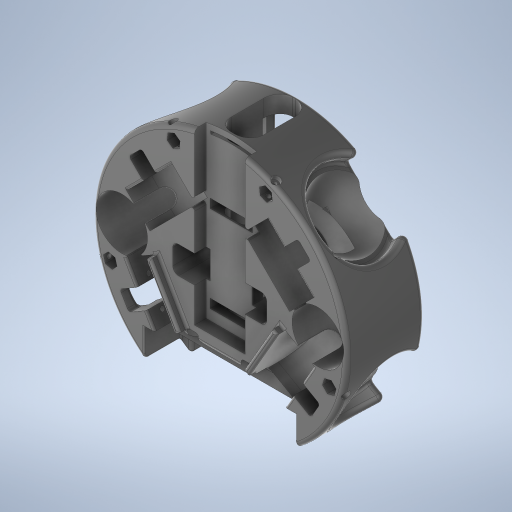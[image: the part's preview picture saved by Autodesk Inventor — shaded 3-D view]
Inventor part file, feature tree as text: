
AUTODESK INVENTOR PART (.ipt)
format: ipt  version: 2023 (Build 270158000, 158)  size: 3,526,144 bytes
history: native  units: mm
features: extrude x76, sketch x76, projected_geometry x35, fillet x19, other x16, chamfer x4, plane x2, mirror x2
ambient origin geometry x8: Origin, YZ Plane, XZ Plane, XY Plane, X Axis, Y Axis, Z Axis, Center Point
bodies: Solid1 (feature_tree)
feature tree (230):
  extrude  "Cilinder"  Depth=54.0mm TaperAngle=0.0deg
  other  "Motor Axis"
  other  "Plano M1"
  other  "Plano M2"
  other  "Plano M3"
  other  "Plano M4"
  extrude  "Roda M1"  Depth=176.0mm
  extrude  "Roda M2"  TaperAngle=60.0deg  [1 undecoded]
  extrude  "Roda M3"  TaperAngle=45.0deg  [1 undecoded]
  extrude  "Roda M4"  TaperAngle=0.0deg  [1 undecoded]
  extrude  "MotorsFitting"  Depth=14.6mm TaperAngle=0.0deg
  fillet  "MotorsCurve"  Radius=55.0mm
  extrude  "Threads M1"  Depth=20.0mm
  extrude  "Threads M2"  Depth=55.0mm
  extrude  "Threads M3"  Depth=20.0mm
  extrude  "Threads M4"  Depth=55.0mm
  extrude  "Threads Head M1"  Depth=20.0mm
  extrude  "Threads Head M2"  Depth=9.4mm
  extrude  "Threads Head M3"  Depth=9.4mm
  extrude  "Threads Head M4"  Depth=23.0mm
  extrude  "Thread Depth M1"  Depth=9.4mm
  extrude  "Thread Depth M2"  Depth=45.0mm
  extrude  "Thread Depth M3"  Depth=45.0mm
  extrude  "Thread Depth M4"  Depth=30.0mm
  extrude  "Threads Nut Head M1"  Depth=32.5mm
  extrude  "Threads Nut Head M2"  Depth=40.0mm TaperAngle=0.0deg
  extrude  "Threads Nut Head M3"  Depth=5.0mm
  extrude  "Threads Nut Head M4"  TaperAngle=0.0deg  [1 undecoded]
  extrude  "Wheel Fitting M1"  Depth=3.0mm
  extrude  "Wheel Fitting M2"  TaperAngle=0.0deg  [1 undecoded]
  extrude  "Wheel Fitting M3"  Depth=30.0mm TaperAngle=360.0deg
  extrude  "Wheel Fitting M4"  Depth=2.0mm
  extrude  "Capacitors"  Depth=6.0mm
  extrude  "Gear Entrance M1"  Depth=19.5mm
  extrude  "Gear Entrance M2"  Depth=10.0mm
  extrude  "Gear Entrance M3"  Depth=2.0mm
  extrude  "Gear Entrance M4"  Depth=3.0mm
  fillet  "Rounding Edges"  Radius=3.0mm
  fillet  "Rounding Motor Entrances"  Radius=6.0mm
  extrude  "Standoff Fitting"  TaperAngle=0.0deg  [1 undecoded]
  extrude  "Standoff Thread M1"  Depth=19.6mm
  extrude  "Standoff Thread M2"  Depth=19.5mm
  extrude  "Standoff Thread M3"  TaperAngle=0.0deg  [1 undecoded]
  extrude  "Standoff Thread M4"  Depth=30.0mm TaperAngle=360.0deg
  other  "Standoff Plane M1"
  other  "Standoff Plane M2"
  other  "Standoff Plane M3"
  other  "Standoff Plane M4"
  extrude  "Standoff Head M1"  Depth=10.0mm
  extrude  "Standoff Head M2"  Depth=2.0mm
  extrude  "Standoff Head M3"  TaperAngle=0.0deg  [1 undecoded]
  extrude  "Standoff Head M4"  Depth=6.0mm
  extrude  "Dribbler Entrance"  Depth=19.5mm
  extrude  "Battery Fitting"  Depth=3.0mm
  fillet  "Motor to Battery Edges"  Radius=3.0mm
  extrude  "Front Kicker"  Depth=11.0mm
  fillet  "Front Edges"  Radius=30.0mm
  extrude  "Cover Inlet"  Depth=10.0mm TaperAngle=0.0deg
  extrude  "Capacitors Holes"  Depth=2.0mm
  extrude  "Dribbler Motor Space"  Depth=6.0mm
  extrude  "IR Holder"  TaperAngle=0.0deg  [1 undecoded]
  fillet  "Dribbler and Kicker Edges"  Radius=19.5mm
  fillet  "Minor Fixes"  Radius=19.5mm
  chamfer  "Dribbler Chanfer"  Distance=30.0mm Angle=360.0deg
  extrude  "Capacitor Cable Fittng 1"  Depth=10.0mm TaperAngle=0.0deg
  fillet  "Capacitor Cable Rounding"  Radius=5.5mm
  extrude  "Special Nut M1"  Depth=5.5mm
  extrude  "Special Nut M2"  Depth=5.5mm
  extrude  "Special Nut M3"  Depth=5.5mm
  extrude  "Special Nut M4"  Depth=5.5mm
  extrude  "Special Nut Cylinder M1"  Depth=5.5mm
  extrude  "Special Nut Cylinder M2"  Depth=5.5mm
  extrude  "Special Nut Cylinder M3"  Depth=5.5mm
  extrude  "Special Nut Cylinder M4"  Depth=4.0mm
  fillet  "Special Nut Rounding"  Radius=4.0mm
  extrude  "Kicker Plate Fit 1"  Depth=4.0mm
  extrude  "Kicker Front Opening"  Depth=17.75mm TaperAngle=0.0deg
  extrude  "Kicker Base Fit"  Depth=4.0mm
  extrude  "Coil and Plinge Fitting"  Depth=4.0mm
  extrude  "Kicker Pkate Plunge Fit"  Depth=17.75mm TaperAngle=0.0deg
  chamfer  "Plunge Entrance 1"  Distance=17.6mm
  chamfer  "Plunge Entrance 2"  Distance=17.6mm
  fillet  "Fillet11"  Radius=15.5mm
  chamfer  "Coil Edges 1"  Distance=17.6mm
  extrude  "Kicker Plate Threads"  Depth=32.0mm
  extrude  "kicker Plate Nut 1"  Depth=35.7mm
  extrude  "Kicker Plate Nut 2"  Depth=68.0mm
  extrude  "Kicker Plunge Fit"  Depth=10.0mm TaperAngle=0.0deg
  fillet  "Kicker Plunge Round"  Radius=12.5mm
  fillet  "Wheel Round"  Radius=14.0mm
  extrude  "Capacitor Cables"  Depth=10.0mm
  fillet  "Capacitor Cable Round 1"  Radius=12.5mm
  fillet  "Capacitor Cable Round 2"  Radius=10.0mm
  extrude  "MotorProtection"  Depth=10.0mm TaperAngle=0.0deg
  fillet  "Motor Protection Round"  Radius=12.5mm
  extrude  "Extrusion86"  Depth=10.0mm
  extrude  "Extrusion87"  Depth=10.0mm TaperAngle=0.0deg
  fillet  "Fillet17"  Radius=12.5mm
  extrude  "Extrusion88"  Depth=10.0mm
  plane  "Work Plane14"
  extrude  "Extrusion89"  Depth=10.0mm TaperAngle=0.0deg
  extrude  "Extrusion91"  Depth=3.0mm
  mirror  "Mirror3"
  fillet  "Fillet18"  Radius=2.0mm
  extrude  "Extrusion92"  Depth=10.0mm
  fillet  "Fillet19"  Radius=22.0mm
  extrude  "Extrusion93"  Depth=10.0mm
  fillet  "Fillet20"  Radius=4.22mm
  extrude  "Extrusion94"  Depth=10.0mm
  extrude  "Extrusion95"  Depth=10.0mm
  other  "Eixo de trabalho1"
  other  "Eixo de trabalho2"
  other  "Eixo de trabalho3"
  other  "Eixo de trabalho4"
  other  "Plano de trabalho16"
  other  "Revolução1"
  other  "Revolução2"
  mirror  "Espelhamento5"
  sketch  "Sketch1"  dims[d0=176.0mm d1=54.0mm d2=0.0mm]
  sketch  "Sketch3"  dims[d3=180.0mm d4=176.0mm]
  sketch  "Sketch4"  dims[d5=60.0deg d6=60.0deg]
  sketch  "Sketch5"  dims[d8=45.0deg d9=45.0deg]
  sketch  "Sketch6"  dims[d10=55.0mm d11=0.0mm]
  sketch  "Sketch7"  dims[d12=20.0mm d13=14.6mm d14=0.0mm d15=55.0mm]
  sketch  "Sketch8"  dims[d16=0.0mm d17=20.0mm]
  sketch  "Sketch9"  dims[d18=14.6mm d19=0.0mm d20=55.0mm]
  sketch  "Sketch10"  dims[d21=0.0mm d22=20.0mm]
  sketch  "Sketch11"  dims[d23=14.6mm d24=0.0mm d25=55.0mm]
  sketch  "Sketch12"  dims[d26=0.0mm d27=20.0mm]
  sketch  "Sketch13"  dims[d28=14.6mm d29=0.0mm d30=9.4mm]
  sketch  "Sketch14"  dims[d32=9.4mm d33=9.4mm]
  sketch  "Sketch15"  dims[d34=23.0mm d35=23.0mm]
  sketch  "Sketch16"  dims[d37=23.0mm d38=9.4mm]
  sketch  "Sketch17"  dims[d39=23.0mm d40=45.0mm]
  sketch  "Sketch18"  dims[d41=45.0mm d42=45.0mm]
  sketch  "Sketch19"  dims[d43=45.0mm d44=30.0mm]
  sketch  "Sketch20"  dims[d45=30.0mm d46=32.5mm]
  sketch  "Sketch21"  dims[d47=32.5mm d48=40.0mm d49=0.0mm]
  sketch  "Sketch22"  dims[d50=22.5mm d51=5.0mm]
  sketch  "Sketch23"  dims[d52=12.5mm d53=0.0mm]
  sketch  "Sketch24"  dims[d54=19.5mm d55=3.0mm]
  sketch  "Sketch25"  dims[d56=19.6mm d58=0.0mm]
  sketch  "Sketch26"  dims[d59=11.0mm d60=30.0mm d62=360.0deg]
  sketch  "Sketch27"  dims[d64=2.0mm d65=2.0mm]
  sketch  "Sketch28"  dims[d66=6.0mm d67=6.0mm]
  sketch  "Sketch29"  dims[d68=19.5mm d69=19.5mm]
  sketch  "Sketch30"  dims[d70=10.0mm d71=0.0mm d72=2.5mm]
  projected_geometry  "Projected Loop1"
  sketch  "Sketch31"  dims[d73=5.0mm d74=2.0mm]
  projected_geometry  "Projected Loop2"
  sketch  "Sketch32"  dims[d75=2.0mm d76=12.5mm d77=3.0mm d78=6.0mm]
  projected_geometry  "Projected Loop3"
  sketch  "Sketch33"  dims[d79=6.0mm d80=0.0mm]
  projected_geometry  "Projected Loop4"
  sketch  "Sketch34"  dims[d81=19.5mm d82=19.6mm]
  sketch  "Sketch35"  dims[d83=19.5mm d84=19.5mm]
  projected_geometry  "Projected Loop5"
  sketch  "Sketch36"  dims[d85=5.0mm d86=0.0mm]
  projected_geometry  "Projected Loop6"
  sketch  "Sketch37"  dims[d87=11.0mm d88=30.0mm d90=360.0deg]
  projected_geometry  "Projected Loop7"
  sketch  "Sketch38"  dims[d92=10.0mm d93=0.0mm d94=5.0mm]
  projected_geometry  "Projected Loop8"
  sketch  "Sketch39"  dims[d95=12.5mm d96=2.0mm]
  sketch  "Sketch40"  dims[d97=2.0mm d98=0.0mm]
  sketch  "Sketch41"  dims[d99=19.5mm d100=6.0mm]
  sketch  "Sketch42"  dims[d101=6.0mm d102=19.5mm]
  sketch  "Sketch43"  dims[d103=19.5mm d104=19.6mm d105=3.0mm]
  sketch  "Sketch44"  dims[d106=0.0mm d107=11.0mm d108=30.0mm d110=360.0deg]
  projected_geometry  "Projected Loop9"
  projected_geometry  "Projected Loop10"
  sketch  "Sketch45"  dims[d112=5.0mm d113=10.0mm d114=0.0mm]
  sketch  "Sketch46"  dims[d115=5.0mm d116=2.0mm]
  projected_geometry  "Projected Loop11"
  projected_geometry  "Projected Loop12"
  sketch  "Sketch48"  dims[d117=2.0mm d118=6.0mm]
  projected_geometry  "Projected Loop14"
  sketch  "Sketch50"  dims[d119=6.0mm d120=0.0mm d121=19.5mm d122=19.5mm]
  projected_geometry  "Projected Loop15"
  sketch  "Sketch59"  dims[d123=19.5mm]
  sketch  "Sketch64"  dims[d124=12.5mm]
  sketch  "Sketch65"  dims[d125=19.6mm]
  projected_geometry  "Projected Loop27"
  sketch  "Sketch66"  dims[d126=3.0mm]
  projected_geometry  "Projected Loop28"
  sketch  "Sketch67"  dims[d127=0.0mm]
  sketch  "Sketch68"  dims[d128=11.0mm d129=30.0mm d131=360.0deg]
  sketch  "Sketch69"  dims[d133=2.5mm d134=10.0mm d135=0.0mm d136=5.5mm]
  sketch  "Sketch70"  dims[d137=5.5mm d138=5.5mm]
  sketch  "Sketch71"  dims[d139=18.0mm d140=0.0mm d141=5.5mm]
  sketch  "Sketch72"  dims[d142=5.5mm d143=5.5mm]
  projected_geometry  "Projected Loop29"
  sketch  "Sketch73"  dims[d144=18.0mm d145=0.0mm d146=5.5mm]
  sketch  "Sketch74"  dims[d147=5.5mm d148=5.5mm]
  projected_geometry  "Projected Loop30"
  sketch  "Sketch75"  dims[d149=18.0mm d150=0.0mm d151=5.5mm]
  projected_geometry  "Projected Loop31"
  sketch  "Sketch76"  dims[d152=5.5mm d153=5.5mm]
  projected_geometry  "Projected Loop32"
  projected_geometry  "Projected Loop33"
  sketch  "Sketch77"  dims[d154=18.0mm d155=0.0mm d156=4.0mm d157=4.0mm]
  projected_geometry  "Projected Loop34"
  projected_geometry  "Projected Loop35"
  projected_geometry  "Projected Loop36"
  projected_geometry  "Projected Loop37"
  sketch  "Sketch78"  dims[d158=17.75mm d159=0.0mm d160=4.0mm]
  sketch  "Sketch80"  dims[d161=4.0mm d162=17.75mm d163=0.0mm]
  projected_geometry  "Projected Loop38"
  projected_geometry  "Projected Loop39"
  projected_geometry  "Projected Loop40"
  projected_geometry  "Projected Loop41"
  sketch  "Sketch81"  dims[d164=4.0mm d165=4.0mm]
  sketch  "Sketch82"  dims[d166=17.75mm d167=0.0mm d168=4.0mm]
  sketch  "Sketch89"  dims[d169=4.0mm d170=17.75mm d171=0.0mm]
  sketch  "Sketch90"  dims[d172=15.5mm]
  sketch  "Sketch92"  dims[d173=32.0mm d174=17.6mm d175=0.0mm]
  sketch  "Sketch93"  dims[d176=15.5mm]
  sketch  "Sketch95"  dims[d177=32.0mm d178=17.6mm d179=0.0mm d180=15.5mm]
  plane  "Work Plane15"
  projected_geometry  "Projected Loop46"
  projected_geometry  "Projected Loop47"
  projected_geometry  "Projected Loop48"
  sketch  "Sketch97"  dims[d181=32.0mm d182=17.6mm d183=0.0mm]
  sketch  "Sketch98"  dims[d184=15.5mm d185=32.0mm]
  projected_geometry  "Projected Loop49"
  projected_geometry  "Projected Loop50"
  projected_geometry  "Projected Loop51"
  sketch  "Sketch99"  dims[d186=17.6mm d187=0.0mm d188=35.7mm]
  sketch  "Esboço100"  dims[d189=4.15mm d190=68.0mm]
  sketch  "Esboço101"  dims[d191=68.0mm d192=50.0mm d193=0.0mm d195=12.5mm d196=14.0mm d197=0.0mm d198=10.0mm d199=12.5mm d200=10.0mm d201=14.0mm d202=0.0mm d203=12.5mm d204=10.0mm d205=14.0mm d206=0.0mm d207=12.5mm d208=10.0mm d209=14.0mm d210=0.0mm d211=3.0mm d212=2.0mm d213=2.0mm d214=2.0mm d215=22.0mm d216=76.0mm d217=4.22mm d218=72.0mm d219=32.0mm d220=4.22mm d221=8.0mm d222=0.0mm d223=3.0mm d224=3.5mm d225=2.436418mm d226=24.0mm d227=0.0mm d228=3.0mm d229=3.5mm d230=2.436418mm d231=24.0mm d232=0.0mm d233=3.0mm d234=3.5mm d235=2.436418mm d236=24.0mm d237=0.0mm d238=3.0mm d239=3.5mm d240=2.436418mm d241=24.0mm d242=0.0mm d243=90.0mm d244=40.0mm d245=0.0mm d246=55.0mm d247=10.0mm d248=0.0mm d249=2.0mm d250=0.0mm d251=2.0mm d252=0.0mm d253=2.0mm d254=0.0mm d255=2.0mm d256=0.0mm d257=2.0mm d258=1.5mm d259=35.0mm d260=120.0mm d261=0.0mm d262=28.5mm d263=8.0mm d264=0.0mm d265=1.5mm d266=-2.0mm d267=-2.0mm d268=-2.0mm d269=-2.0mm d270=5.5mm d271=4.0mm d272=0.0mm d273=5.5mm d274=4.0mm d275=0.0mm d276=5.5mm d277=4.0mm d278=0.0mm d279=5.5mm d280=4.0mm d281=0.0mm d282=56.5mm d283=12.5mm d284=0.0mm d285=17.0mm d286=10.0mm d287=0.0mm d288=2.0mm d289=3.0mm d299=82.0mm d300=17.453293mm d301=3.490659mm d302=84.0mm d303=17.453293mm d304=3.490659mm d305=8.0mm d306=0.0mm d307=0.4mm d308=22.0mm d309=22.0mm d310=10.0mm d311=0.0mm d317=90.0mm d318=14.0mm d319=0.0mm d320=0.0mm d321=11.0mm d322=0.0mm d327=3.75mm d328=17.11mm d329=0.0mm d330=24.43461mm d331=7.1mm d332=0.0mm d355=2.0mm d356=2.0mm d357=45.0deg d358=3.0mm d359=2.0mm d396=5.5mm d397=10.0mm d398=23.0mm d399=16.0mm d400=56.0mm d401=0.0mm d402=5.5mm d403=0.0mm d404=1.5mm d429=8.1mm d430=16.1mm d431=6.0mm d432=3.0mm d433=0.0mm d434=0.0mm d435=16.1mm d436=8.1mm d437=6.0mm d438=3.0mm d439=0.0mm d440=0.0mm d441=16.1mm d442=8.1mm d443=6.0mm d444=3.0mm d445=0.0mm d446=0.0mm d447=8.1mm d448=16.1mm d449=6.0mm d450=3.0mm d451=0.0mm d452=0.0mm d453=8.1mm d454=5.75mm d455=0.0mm d456=8.1mm d457=5.75mm d458=0.0mm d459=8.1mm d460=5.75mm d461=0.0mm d462=8.1mm d463=5.75mm d464=0.0mm d465=0.9mm d466=29.2mm d467=135.0mm d468=0.0mm d469=14.6mm d470=76.25mm d471=43.2mm d472=7.1mm d473=0.0mm d474=43.2mm d475=7.1mm d476=0.0mm d477=34.5mm d478=79.5mm d479=6.0mm d480=0.0mm d481=30.9mm d482=41.0mm d483=0.0mm d485=29.2mm d486=6.2mm d490=46.1mm d491=0.0mm d492=29.2mm d493=6.2mm d494=3.6mm d495=3.6mm d496=44.8mm d497=0.0mm d498=7.0mm d499=0.0mm d500=6.4mm d501=3.6mm d502=45.0deg d503=6.4mm d504=3.6mm d505=45.0deg d507=10.0mm d508=7.5mm d509=4.6mm d510=60.0deg d511=3.0mm d512=3.0mm d513=18.0mm d514=18.0mm d515=3.0mm d516=3.0mm d517=18.0mm d518=18.0mm d519=3.55mm d520=3.55mm d521=3.55mm d522=3.55mm d523=12.0mm d524=0.0mm d525=5.6mm d526=2.4mm d527=5.6mm d528=2.4mm d529=3.0mm d530=3.0mm d531=1.3mm d532=1.3mm d533=39.8mm d534=0.0mm d535=60.0deg d536=60.0deg d537=120.0deg d538=120.0deg d539=60.0deg d540=60.0deg d541=120.0deg d542=120.0deg d543=10.0mm d544=0.0mm d545=22.0mm d546=20.0mm d547=11.0mm d548=12.5mm d549=10.0mm d550=0.0mm d551=10.0mm d552=3.0mm d553=2.0mm d554=3.0mm d555=18.0mm d556=19.0mm d557=18.0mm d558=19.0mm d559=23.6mm d560=23.6mm d561=7.5mm d562=7.5mm d563=47.0mm d564=0.0mm d565=2.0mm d566=2.0mm d567=4.0mm d568=5.0mm d609=0.0mm d611=5.0mm d612=0.0mm d613=3.75mm d614=0.0mm d616=0.0mm d617=5.0mm d618=3.75mm d619=6.0mm d620=0.0mm d621=1.75mm d622=0.75mm d623=5.5mm d624=9.5mm d625=9.25mm d626=25.9mm d627=8.5mm d628=0.0mm d632=3.0mm d633=0.0mm d636=7.4mm d637=0.0mm d638=3.0mm d639=3.0mm d640=4.0mm d641=3.75mm d642=131.25mm d643=0.0mm d644=-8.0mm d645=5.5mm d646=10.0mm d647=0.0mm d650=10.0mm d651=10.0mm d653=16.0mm d654=2.5mm d655=0.0mm d656=1.0mm d657=2.0mm d664=1.0mm d665=0.0mm d666=19.9mm d667=0.5mm d668=53.9mm d669=25.0mm d670=10.25mm d671=26.12407mm d672=8.0mm d673=90.0deg d674=90.0deg d675=90.0deg d676=90.0deg d677=90.0deg d678=90.0deg d679=90.0deg d680=4.0mm d681=2.0mm d682=29.2mm d683=10.0mm d684=0.0mm d685=2.0mm d686=0.5mm d687=3.0mm d688=3.0mm d689=6.5mm d691=6.5mm d692=4.0mm d693=10.0mm d694=0.0mm d695=5.5mm d696=5.5mm d697=2.0mm d698=2.1mm d699=0.0mm d700=0.0mm d701=4.0mm d702=0.0mm d703=50.0mm d704=82.5mm d705=90.0deg d706=50.0mm d707=82.5mm d708=90.0deg]
note: 9 required parameter values undecoded (feature->parameter linkage not recoverable at this tier; creation-order binding heuristic only, values carry confidence <= 0.55)
